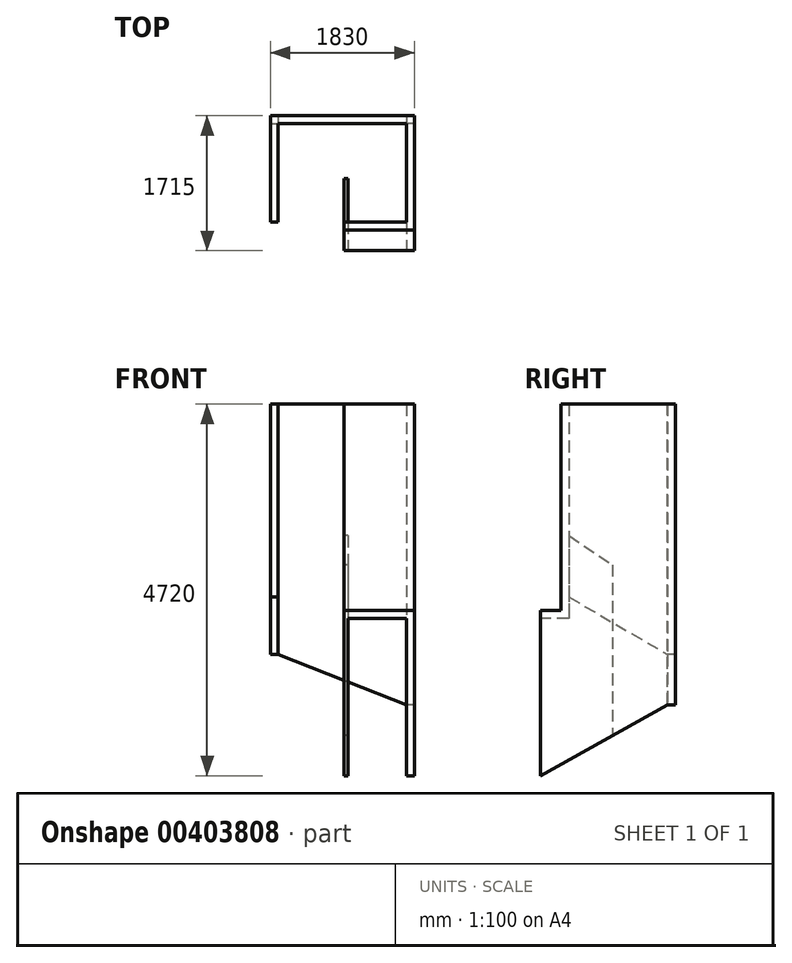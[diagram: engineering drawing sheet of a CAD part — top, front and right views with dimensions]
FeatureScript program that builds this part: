
annotation { "Feature Type Name" : "Feature", "Feature Type Description" : "" }
export const myFeature = defineFeature(function(context is Context, id is Id, definition is map)
    precondition{}
    {
        {
            var Q0;
            Q0=qCreatedBy(makeId("Front.planeOp"),FACE);
            var sketch = newSketch(context, id + "F0", { "sketchPlane" : qUnion([Q0])});
            skLineSegment(sketch, "E0", {"start": v(0, 0) * mm, "end": v(-1630, 0) * mm});
            skLineSegment(sketch, "E1", {"start": v(-1630, 0) * mm, "end": v(-1630, -3180) * mm});
            skLineSegment(sketch, "E2", {"start": v(-1630, -3180) * mm, "end": v(0, -3820) * mm});
            skLineSegment(sketch, "E3", {"start": v(0, -3820) * mm, "end": v(0, 0) * mm});
            skSolve(sketch);
        }
        {
            var Q0;
            Q0 = qSketchRegion(id + "F0", true);
            extrude(context, id + "F1", {"entities" : qUnion([Q0]), "oppositeDirection" : true, "depth" : 100 * mm});
        }
        {
            var Q0;
            Q0=makeQuery(id+"F1.opExtrude","SWEPT_FACE",FACE,{"disambiguationData":[OSD([sQuery(id+"F0.wireOp",EDGE,"E1")])]});
            var sketch = newSketch(context, id + "F2", { "sketchPlane" : qUnion([Q0])});
            skLineSegment(sketch, "E4", {"start": v(-100, 0) * mm, "end": v(1250, 0) * mm});
            skLineSegment(sketch, "E5", {"start": v(1250, 0) * mm, "end": v(1250, -2450) * mm});
            skLineSegment(sketch, "E6", {"start": v(1250, -2450) * mm, "end": v(0, -3180) * mm});
            skLineSegment(sketch, "E7", {"start": v(0, -3180) * mm, "end": v(-100, -3180) * mm});
            skLineSegment(sketch, "E8", {"start": v(-100, -3180) * mm, "end": v(-100, 0) * mm});
            skSolve(sketch);
        }
        {
            var Q0;
            Q0 = qSketchRegion(id + "F2", true);
            extrude(context, id + "F3", {"entities" : qUnion([Q0]), "operationType" : NewBodyOperationType.ADD, "depth" : 100 * mm});
        }
        {
            var Q0;
            Q0=makeQuery(id+"F1.opExtrude","SWEPT_FACE",FACE,{"disambiguationData":[OSD([sQuery(id+"F0.wireOp",EDGE,"E3")])]});
            var sketch = newSketch(context, id + "F4", { "sketchPlane" : qUnion([Q0])});
            skLineSegment(sketch, "E9", {"start": v(100, 0) * mm, "end": v(-1250, 0) * mm});
            skPoint(sketch, "E9.endSnap0", {"position": v(50, 0) * mm});
            skLineSegment(sketch, "E10", {"start": v(-1250, 0) * mm, "end": v(-1250, -2720) * mm});
            skLineSegment(sketch, "E11", {"start": v(0, -3820) * mm, "end": v(100, -3820) * mm});
            skLineSegment(sketch, "E12", {"start": v(100, -3820) * mm, "end": v(100, 0) * mm});
            skLineSegment(sketch, "E13", {"start": v(-1250, -2720) * mm, "end": v(-1615, -2720) * mm});
            skLineSegment(sketch, "E14", {"start": v(-1615, -2720) * mm, "end": v(-1615, -4720) * mm});
            skLineSegment(sketch, "E15", {"start": v(-1615, -4720) * mm, "end": v(0, -3820) * mm});
            skSolve(sketch);
        }
        {
            var Q0;
            Q0 = qSketchRegion(id + "F4", true);
            extrude(context, id + "F5", {"entities" : qUnion([Q0]), "operationType" : NewBodyOperationType.ADD, "depth" : 100 * mm});
        }
        {
            var Q0;
            Q0=makeQuery(id+"F5.opExtrude","CAP_FACE",FACE,{"disambiguationData":[OSD([sQuery(id+"F4.wireOp",EDGE,"E9"),sQuery(id+"F4.wireOp",EDGE,"E10"),sQuery(id+"F4.wireOp",EDGE,"E11"),sQuery(id+"F4.wireOp",EDGE,"E12"),sQuery(id+"F4.wireOp",EDGE,"E13"),sQuery(id+"F4.wireOp",EDGE,"E14"),sQuery(id+"F4.wireOp",EDGE,"E15")])],"isStart":true});
            var sketch = newSketch(context, id + "F6", { "sketchPlane" : qUnion([Q0])});
            skLineSegment(sketch, "E16.1", {"start": v(1250, 0) * mm, "end": v(1250, -2720) * mm});
            skLineSegment(sketch, "E17.0", {"start": v(1250, -2720) * mm, "end": v(1615, -2720) * mm});
            skPoint(sketch, "E17.1", {"position": v(1432.5, -2720) * mm});
            skLineSegment(sketch, "E18.0", {"start": v(1350, -2620) * mm, "end": v(1615, -2620) * mm});
            skLineSegment(sketch, "E18.1", {"start": v(1350, 0) * mm, "end": v(1350, -2620) * mm});
            skLineSegment(sketch, "E19", {"start": v(1350, 0) * mm, "end": v(1250, 0) * mm});
            skLineSegment(sketch, "E20", {"start": v(1615, -2620) * mm, "end": v(1615, -2720) * mm});
            skSolve(sketch);
        }
        {
            var Q0;
            Q0 = qSketchRegion(id + "F6", true);
            var Q1;
            Q1=makeQuery(id+"F5.opExtrude","CAP_FACE",FACE,{"disambiguationData":[OSD([sQuery(id+"F4.wireOp",EDGE,"E9"),sQuery(id+"F4.wireOp",EDGE,"E10"),sQuery(id+"F4.wireOp",EDGE,"E11"),sQuery(id+"F4.wireOp",EDGE,"E12"),sQuery(id+"F4.wireOp",EDGE,"E13"),sQuery(id+"F4.wireOp",EDGE,"E14"),sQuery(id+"F4.wireOp",EDGE,"E15")])],"isStart":false});
            extrude(context, id + "F7", {"entities" : qUnion([Q0]), "operationType" : NewBodyOperationType.ADD, "endBound" : BoundingType.UP_TO_SURFACE, "oppositeDirection" : true, "endBoundEntityFace" : qUnion([Q1]), "depth" : 25 * mm});
        }
        {
            var Q0;
            Q0 = qSketchRegion(id + "F6", true);
            extrude(context, id + "F8", {"entities" : qUnion([Q0]), "operationType" : NewBodyOperationType.ADD, "depth" : 790 * mm});
        }
        {
            var Q0;
            Q0=makeQuery(id+"F8.opExtrude","CAP_FACE",FACE,{"disambiguationData":[OSD([sQuery(id+"F6.wireOp",EDGE,"E16.1"),sQuery(id+"F6.wireOp",EDGE,"E17.0"),sQuery(id+"F6.wireOp",EDGE,"E18.0"),sQuery(id+"F6.wireOp",EDGE,"E18.1"),sQuery(id+"F6.wireOp",EDGE,"E19"),sQuery(id+"F6.wireOp",EDGE,"E20")])],"isStart":false});
            var sketch = newSketch(context, id + "F9", { "sketchPlane" : qUnion([Q0])});
            skLineSegment(sketch, "E21", {"start": v(1250, -1670) * mm, "end": v(700, -2040) * mm});
            skLineSegment(sketch, "E22", {"start": v(700, -2040) * mm, "end": v(700, -4210.1) * mm});
            skLineSegment(sketch, "E23.0", {"start": v(1615, -4720) * mm, "end": v(700, -4210.1) * mm});
            skLineSegment(sketch, "E24", {"start": v(1250, -1670) * mm, "end": v(1250, -2720) * mm});
            skLineSegment(sketch, "E25", {"start": v(1250, -2720) * mm, "end": v(1615, -2720) * mm});
            skLineSegment(sketch, "E26", {"start": v(1615, -2720) * mm, "end": v(1615, -4720) * mm});
            skPoint(sketch, "E27.orphan", {"position": v(0, -3820) * mm});
            skSolve(sketch);
        }
        {
            var Q0;
            Q0 = qSketchRegion(id + "F9", true);
            extrude(context, id + "F10", {"entities" : qUnion([Q0]), "operationType" : NewBodyOperationType.ADD, "oppositeDirection" : true, "depth" : 50 * mm});
        }
    });
